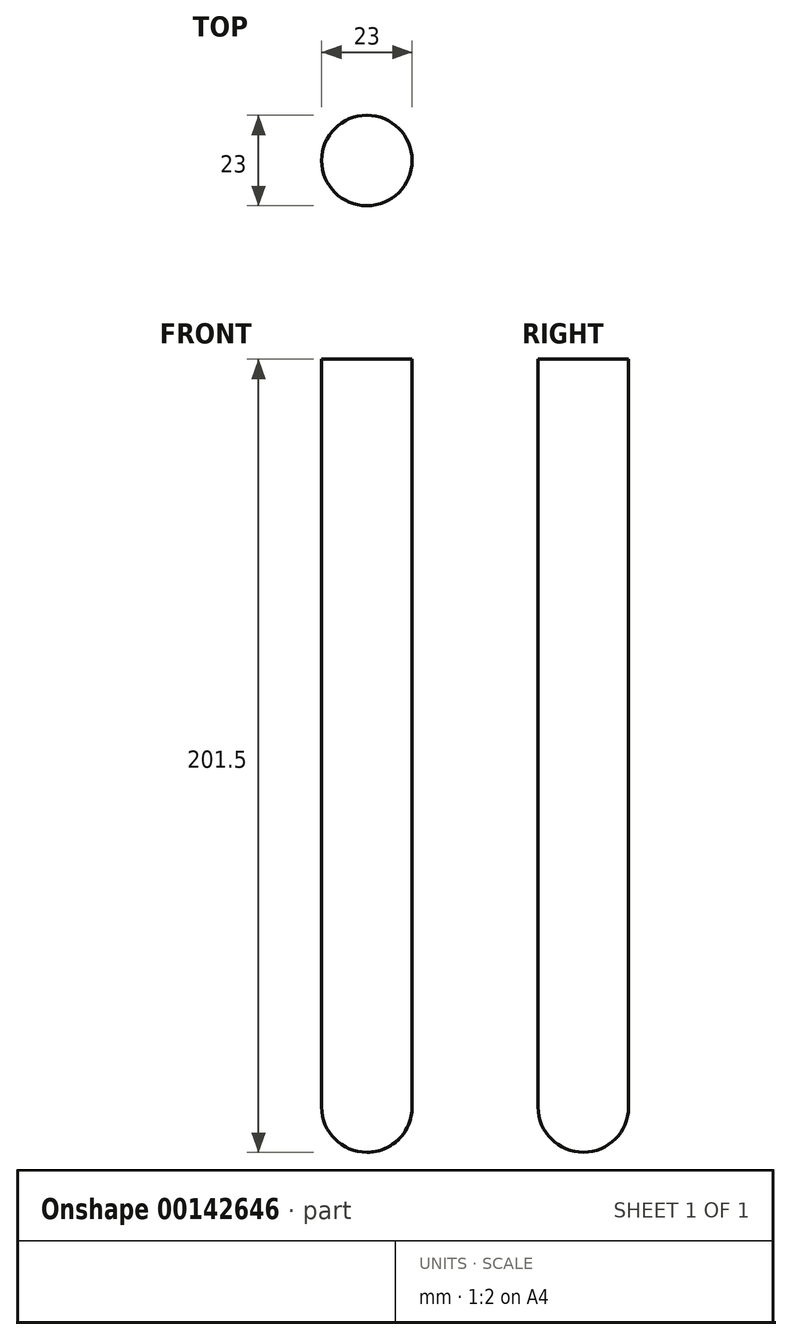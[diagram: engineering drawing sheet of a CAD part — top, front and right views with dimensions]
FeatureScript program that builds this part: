
annotation { "Feature Type Name" : "Feature", "Feature Type Description" : "" }
export const myFeature = defineFeature(function(context is Context, id is Id, definition is map)
    precondition{}
    {
        {
            var Q0;
            Q0=qCreatedBy(makeId("Top.planeOp"),FACE);
            var sketch = newSketch(context, id + "F0", { "sketchPlane" : qUnion([Q0])});
            skCircle(sketch, "E0", {"center": v(0, 0) * mm, "radius": 11.5 * mm});
            skSolve(sketch);
        }
        {
            var Q0;
            Q0=makeQuery(id+"F0.imprint","IMPRINT",FACE,{"disambiguationData":[TD([[makeQuery(id+"F0.imprint","IMPRINT",EDGE,{"derivedFrom":sQuery(id+"F0.wireOp",EDGE,"E0")}),1.0]])]});
            extrude(context, id + "F1", {"entities" : qUnion([Q0]), "depth" : 190 * mm});
        }
        {
            var Q0;
            Q0=qCreatedBy(makeId("Front.planeOp"),FACE);
            var sketch = newSketch(context, id + "F2", { "sketchPlane" : qUnion([Q0])});
            skLineSegment(sketch, "E1.0.0", {"start": v(11.5, 0) * mm, "end": v(0, 0) * mm});
            skArc(sketch, "E2", {"start": v(0, -11.5) * mm, "mid": v(8.13, -8.13) * mm, "end": v(11.5, 0) * mm});
            skLineSegment(sketch, "E3", {"start": v(0, 0) * mm, "end": v(0, -11.5) * mm, "construction": true});
            skPoint(sketch, "E4.orphan", {"position": v(-11.5, 0) * mm});
            skLineSegment(sketch, "E5", {"start": v(0, 0) * mm, "end": v(0, -11.5) * mm});
            skSolve(sketch);
        }
        {
            var Q0;
            Q0=makeQuery(id+"F2.imprint","IMPRINT",FACE,{"disambiguationData":[TD([[makeQuery(id+"F2.imprint","IMPRINT",EDGE,{"derivedFrom":sQuery(id+"F2.wireOp",EDGE,"E1.0.0")}),1.0]])]});
            var Q1;
            Q1=sQuery(id+"F2.wireOp",EDGE,"E5");
            revolve(context, id + "F3", {"operationType" : NewBodyOperationType.ADD, "entities" : qUnion([Q0]), "axis" : qUnion([Q1]), "revolveType" : RevolveType.FULL});
        }
    });
